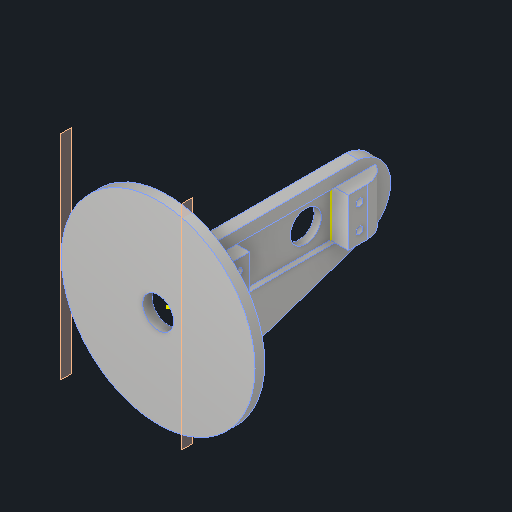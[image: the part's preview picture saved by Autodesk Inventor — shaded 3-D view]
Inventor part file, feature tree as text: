
AUTODESK INVENTOR PART (.ipt)
format: ipt  version: 2023.4 (Build 274418000, 418)  size: 357,888 bytes
history: native  units: mm
features: sketch x16, extrude x10, thread x4, plane x2, fillet x1
ambient origin geometry x8: Origin, YZ Plane, XZ Plane, XY Plane, X Axis, Y Axis, Z Axis, Center Point
bodies: Solid1 (feature_tree)
feature tree (33):
  extrude  "Extrusion1"  Depth=4.0mm TaperAngle=0.0deg
  plane  "Work Plane2"
  extrude  "Extrusion4"  Depth=5.0mm
  extrude  "Extrusion5"  Depth=50.0mm
  extrude  "Extrusion8"  Depth=5.0mm TaperAngle=0.0deg
  extrude  "Extrusion9"  Depth=6.0mm TaperAngle=0.0deg
  extrude  "Extrusion10"  Depth=19.8mm
  fillet  "Fillet1"  Radius=2.0mm
  extrude  "Extrusion11"  Depth=19.8mm
  extrude  "Extrusion12"  Depth=5.5mm TaperAngle=0.0deg
  sketch  "Sketch14"  dims[d15=12.8mm d16=6.0mm d17=0.0mm]
  extrude  "Extrusion13"  Depth=5.5mm
  thread  "Thread1"  [1 undecoded]
  thread  "Thread2"  [1 undecoded]
  thread  "Thread3"  [1 undecoded]
  thread  "Thread4"  [1 undecoded]
  sketch  "Sketch16"  dims[d28=10.0mm d29=19.8mm]
  sketch  "Sketch17"  dims[d30=5.5mm d31=0.0mm d32=5.5mm d33=0.0mm]
  sketch  "Sketch18"  dims[d34=10.0mm d35=9.9mm d36=10.0mm d38=13.404mm d39=5.5mm d40=0.0mm d43=2.95mm]
  sketch  "Sketch19"  dims[d44=2.95mm d45=10.0mm d46=0.0mm]
  sketch  "Sketch20"  dims[d49=2.95mm]
  extrude  "Extrusion14"  Depth=10.0mm TaperAngle=0.0deg
  sketch  "Sketch22"  dims[d51=10.0mm d52=0.0mm]
  sketch  "Sketch23"  dims[d53=10.0mm d54=0.0mm]
  sketch  "Sketch24"  dims[d55=10.0mm d56=0.0mm]
  sketch  "Sketch25"  dims[d57=10.0mm d58=0.0mm d59=10.0mm d60=0.0mm d61=12.8mm d62=10.0mm d63=0.0mm d37=0.0mm d41=0.872665mm]
  plane  "Work Plane1"
  sketch  "Sketch2"  dims[d0=80.0mm d1=4.0mm d2=0.0mm]
  sketch  "Sketch9"  dims[d3=50.0mm d4=5.0mm]
  sketch  "Sketch10"  dims[d5=50.0mm d6=20.0mm]
  sketch  "Sketch11"  dims[d8=15.0mm d13=5.0mm d14=0.0mm]
  sketch  "Sketch15"  dims[d24=40.6mm d25=19.8mm d26=2.0mm d27=0.0mm]
  sketch  "Sketch21"  dims[d50=2.95mm]
note: 4 required parameter values undecoded (feature->parameter linkage not recoverable at this tier; creation-order binding heuristic only, values carry confidence <= 0.55)
